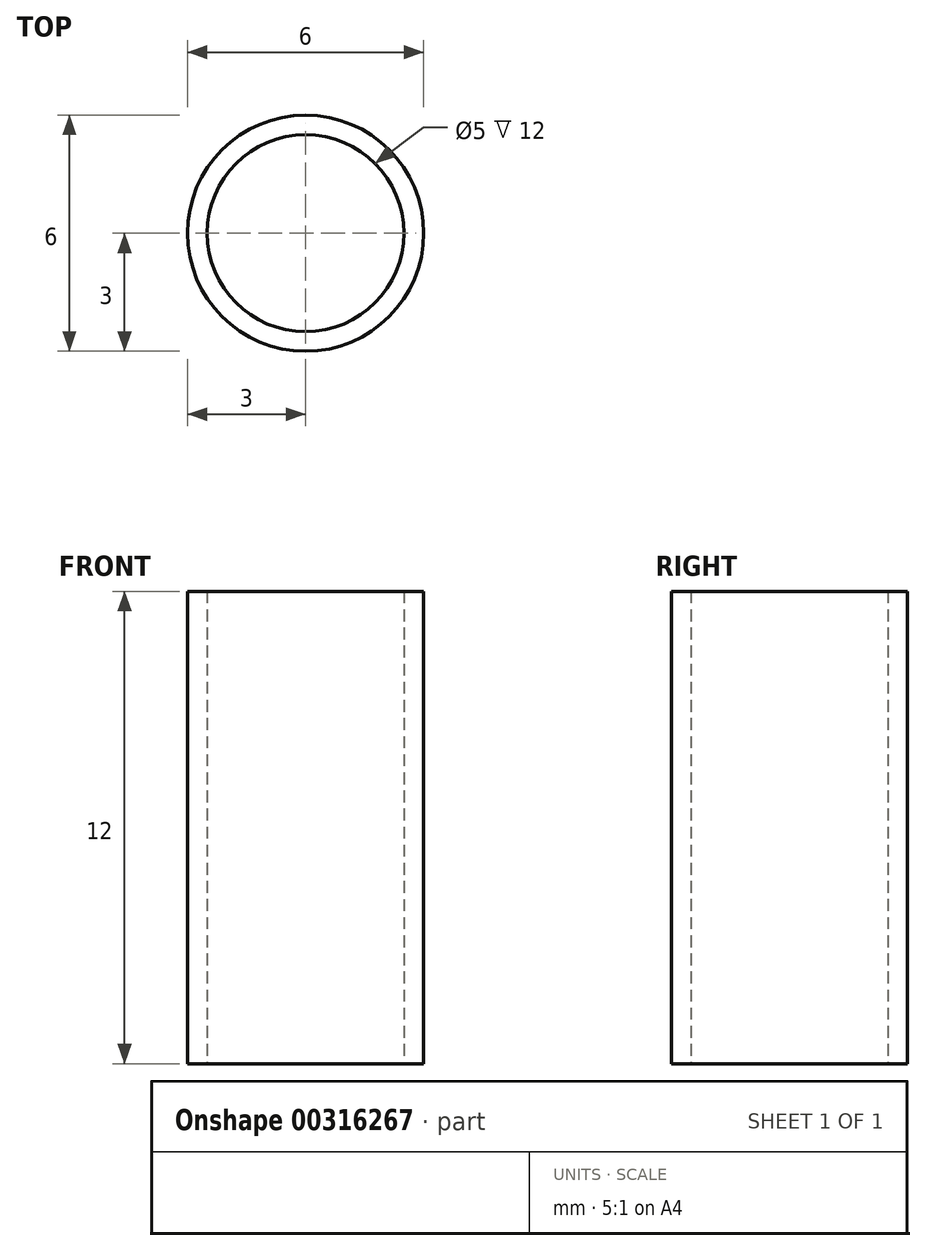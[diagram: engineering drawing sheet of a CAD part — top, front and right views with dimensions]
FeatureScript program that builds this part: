
annotation { "Feature Type Name" : "Feature", "Feature Type Description" : "" }
export const myFeature = defineFeature(function(context is Context, id is Id, definition is map)
    precondition{}
    {
        {
            var Q0;
            Q0=qCreatedBy(makeId("Top.planeOp"),FACE);
            var sketch = newSketch(context, id + "F0", { "sketchPlane" : qUnion([Q0])});
            skCircle(sketch, "E0", {"center": v(0, 0) * mm, "radius": 2.5 * mm});
            skCircle(sketch, "E1", {"center": v(0, 0) * mm, "radius": 3 * mm});
            skSolve(sketch);
        }
        {
            var Q0;
            Q0 = qSketchRegion(id + "F0", true);
            extrude(context, id + "F1", {"entities" : qUnion([Q0]), "depth" : 12 * mm});
        }
    });
